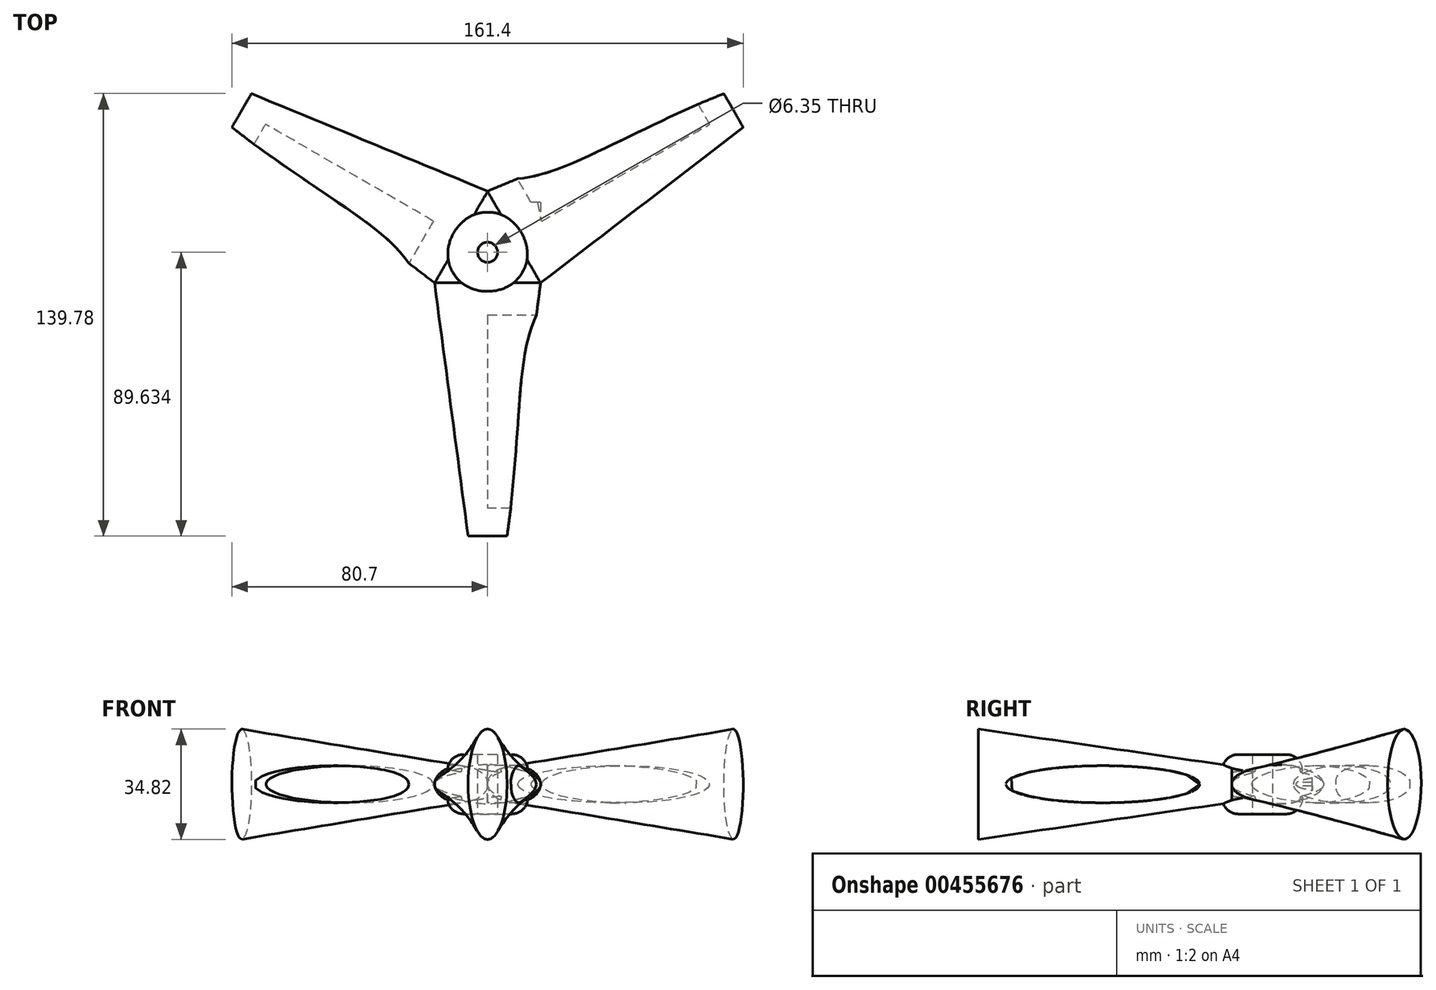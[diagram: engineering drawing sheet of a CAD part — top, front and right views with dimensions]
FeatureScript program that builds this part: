
annotation { "Feature Type Name" : "Feature", "Feature Type Description" : "" }
export const myFeature = defineFeature(function(context is Context, id is Id, definition is map)
    precondition{}
    {
        {
            var Q0;
            Q0=qCreatedBy(makeId("Front.planeOp"),FACE);
            var sketch = newSketch(context, id + "F0", { "sketchPlane" : qUnion([Q0])});
            skEllipse(sketch, "E0", {"center": v(0, 0) * mm, "majorRadius": 16.75 * mm, "minorRadius": 5.75 * mm, "majorAxis": v(-1, 0)});
            skSolve(sketch);
        }
        {
            var Q0;
            Q0=qCreatedBy(makeId("Right.planeOp"),FACE);
            cPlane(context, id + "F1", {"entities" : qUnion([Q0]), "cplaneType" : CPlaneType.OFFSET, "offset" : 25.4 * mm, "width" : 152.4 * mm, "height" : 152.4 * mm});
        }
        {
            var Q0;
            Q0=qCreatedBy(makeId("Front.planeOp"),FACE);
            cPlane(context, id + "F2", {"entities" : qUnion([Q0]), "cplaneType" : CPlaneType.OFFSET, "offset" : 80 * mm, "width" : 152.4 * mm, "height" : 152.4 * mm});
        }
        {
            var Q0;
            Q0=qCreatedBy(id+"F2.planeOp",FACE);
            var sketch = newSketch(context, id + "F3", { "sketchPlane" : qUnion([Q0])});
            skEllipse(sketch, "E1", {"center": v(0, 0) * mm, "majorRadius": 17.41 * mm, "minorRadius": 6.16 * mm, "majorAxis": v(0, 1)});
            skSolve(sketch);
        }
        {
            var Q0;
            Q0=makeQuery(id+"F3.imprint","IMPRINT",FACE,{"disambiguationData":[TD([[makeQuery(id+"F3.imprint","IMPRINT",EDGE,{"derivedFrom":sQuery(id+"F3.wireOp",EDGE,"E1")}),1.0]])]});
            var Q1;
            Q1=makeQuery(id+"F0.imprint","IMPRINT",FACE,{"disambiguationData":[TD([[makeQuery(id+"F0.imprint","IMPRINT",EDGE,{"derivedFrom":sQuery(id+"F0.wireOp",EDGE,"E0")}),1.0]])]});
            loft(context, id + "F4", {"sheetProfilesArray" : [{ "sheetProfileEntities" : qUnion([Q0]) }, { "sheetProfileEntities" : qUnion([Q1]) }]});
        }
        {
            var Q0;
            Q0=qCreatedBy(id+"F1.planeOp",FACE);
            var sketch = newSketch(context, id + "F5", { "sketchPlane" : qUnion([Q0])});
            skEllipse(sketch, "E2", {"center": v(-40.71, 0) * mm, "majorRadius": 30.57 * mm, "minorRadius": 5.86 * mm, "majorAxis": v(1, 0)});
            skSolve(sketch);
        }
        {
            var Q0;
            Q0=makeQuery(id+"F5.imprint","IMPRINT",FACE,{"disambiguationData":[TD([[makeQuery(id+"F5.imprint","IMPRINT",EDGE,{"derivedFrom":sQuery(id+"F5.wireOp",EDGE,"E2")}),1.0]])]});
            extrude(context, id + "F6", {"entities" : qUnion([Q0]), "operationType" : NewBodyOperationType.REMOVE, "oppositeDirection" : true, "depth" : 25.4 * mm, "offsetDistance" : 25.4 * mm});
        }
        {
            var Q0;
            Q0=qCreatedBy(makeId("Top.planeOp"),FACE);
            var sketch = newSketch(context, id + "F7", { "sketchPlane" : qUnion([Q0])});
            skCircle(sketch, "E3", {"center": v(0, 9.62) * mm, "radius": 3.18 * mm});
            skCircle(sketch, "E4", {"center": v(0, 9.62) * mm, "radius": 12.68 * mm});
            skSolve(sketch);
        }
        {
            var Q0;
            Q0=makeQuery(id+"F4.opLoft","SWEPT_BODY",BODY,{"disambiguationData":[OSD([makeQuery(id+"F0.imprint","IMPRINT",FACE,{"disambiguationData":[TD([[makeQuery(id+"F0.imprint","IMPRINT",EDGE,{"derivedFrom":sQuery(id+"F0.wireOp",EDGE,"E0")}),1.0]])]}),makeQuery(id+"F3.imprint","IMPRINT",FACE,{"disambiguationData":[TD([[makeQuery(id+"F3.imprint","IMPRINT",EDGE,{"derivedFrom":sQuery(id+"F3.wireOp",EDGE,"E1")}),1.0]])]})])]});
            var Q1;
            Q1=sQuery(id+"F7.wireOp",EDGE,"E4");
            circularPattern(context, id + "F8", {"entities" : qUnion([Q0]), "axis" : qUnion([Q1]), "angle" : 360 * degree, "instanceCount" : 3, "equalSpace" : true});
        }
        {
            var Q0;
            Q0=makeQuery(id+"F7.imprint","IMPRINT",FACE,{"disambiguationData":[TD([[makeQuery(id+"F7.imprint","IMPRINT",EDGE,{"derivedFrom":sQuery(id+"F7.wireOp",EDGE,"E3")}),-1.0]])]});
            extrude(context, id + "F9", {"entities" : qUnion([Q0]), "operationType" : NewBodyOperationType.ADD, "depth" : 9.4 * mm, "offsetDistance" : 25.4 * mm, "hasSecondDirection" : true, "secondDirectionOppositeDirection" : true, "secondDirectionDepth" : 9.4 * mm});
        }
        {
            var Q0;
            Q0=makeQuery(id+"F9.opExtrude","CAP_EDGE",EDGE,{"disambiguationData":[OSD([sQuery(id+"F7.wireOp",EDGE,"E4")])],"isStart":true});
            var Q1;
            Q1=makeQuery(id+"F9.opExtrude","CAP_EDGE",EDGE,{"disambiguationData":[OSD([sQuery(id+"F7.wireOp",EDGE,"E4")])],"isStart":false});
            fillet(context, id + "F10", {"entities" : qUnion([Q0, Q1]), "radius" : 5.08 * mm, "tangentPropagation" : true, "allowEdgeOverflow" : false});
        }
        {
            var Q0;
            {var subQ0=sQuery(id+"F0.wireOp",EDGE,"E0");var subQ2=makeQuery(id+"F4.opLoft","CAP_FACE",FACE,{"disambiguationData":[OSD([makeQuery(id+"F0.imprint","IMPRINT",FACE,{"disambiguationData":[TD([[makeQuery(id+"F0.imprint","IMPRINT",EDGE,{"derivedFrom":subQ0}),1.0]])]})])],"isStart":true});Q0=makeQuery(id+"F9.boolean.opBoolean","SPLIT",FACE,{"disambiguationData":[TD([subQ2])],"derivedFrom":makeQuery(id+"F8.opPattern","COPY",FACE,{"derivedFrom":subQ2,"instanceName":"2"})});}
            var Q1;
            {var subQ0=sQuery(id+"F0.wireOp",EDGE,"E0");var subQ1=makeQuery(id+"F4.opLoft","CAP_FACE",FACE,{"disambiguationData":[OSD([makeQuery(id+"F0.imprint","IMPRINT",FACE,{"disambiguationData":[TD([[makeQuery(id+"F0.imprint","IMPRINT",EDGE,{"derivedFrom":subQ0}),1.0]])]})])],"isStart":true});Q1=makeQuery(id+"F9.boolean.opBoolean","SPLIT",FACE,{"disambiguationData":[TD([makeQuery(id+"F8.opPattern","COPY",FACE,{"derivedFrom":subQ1,"instanceName":"1"})])],"derivedFrom":makeQuery(id+"F8.opPattern","COPY",FACE,{"derivedFrom":subQ1,"instanceName":"2"})});}
            extrude(context, id + "F11", {"entities" : qUnion([Q0, Q1]), "operationType" : NewBodyOperationType.ADD, "depth" : 18.03 * mm, "offsetDistance" : 25.4 * mm});
        }
        {
            var Q0;
            {var subQ0=sQuery(id+"F0.wireOp",EDGE,"E0");var subQ2=makeQuery(id+"F4.opLoft","CAP_FACE",FACE,{"disambiguationData":[OSD([makeQuery(id+"F0.imprint","IMPRINT",FACE,{"disambiguationData":[TD([[makeQuery(id+"F0.imprint","IMPRINT",EDGE,{"derivedFrom":subQ0}),1.0]])]})])],"isStart":true});Q0=makeQuery(id+"F9.boolean.opBoolean","SPLIT",FACE,{"disambiguationData":[TD([makeQuery(id+"F8.opPattern","COPY",FACE,{"derivedFrom":subQ2,"instanceName":"1"})])],"derivedFrom":subQ2});}
            extrude(context, id + "F12", {"entities" : qUnion([Q0]), "operationType" : NewBodyOperationType.ADD, "depth" : 25.4 * mm, "offsetDistance" : 25.4 * mm});
        }
    });
